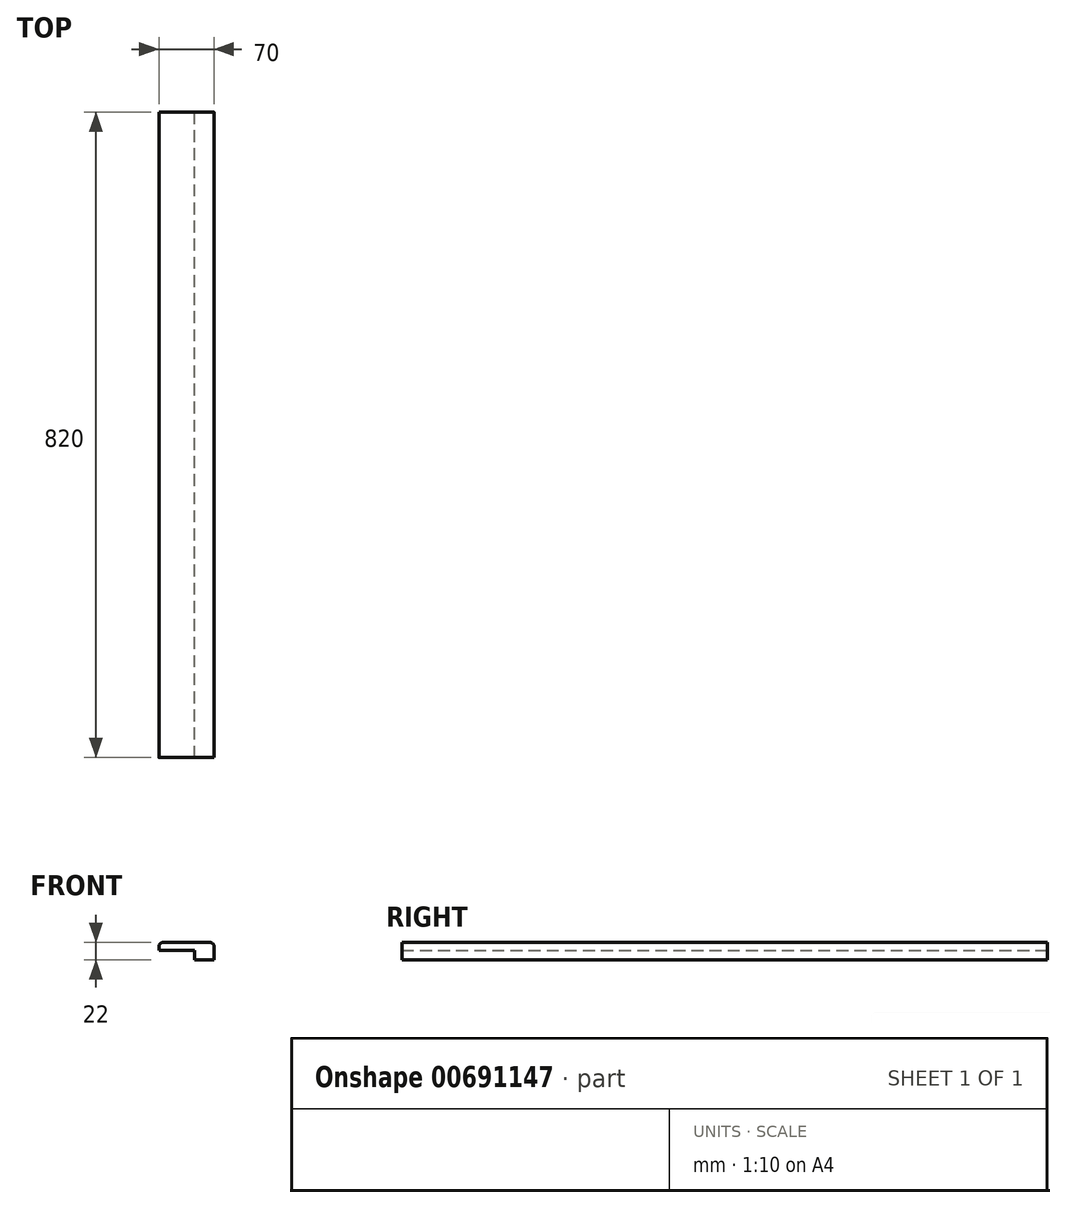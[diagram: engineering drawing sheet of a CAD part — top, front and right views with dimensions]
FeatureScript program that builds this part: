
annotation { "Feature Type Name" : "Feature", "Feature Type Description" : "" }
export const myFeature = defineFeature(function(context is Context, id is Id, definition is map)
    precondition{}
    {
        {
            var Q0;
            Q0=qCreatedBy(makeId("Front.planeOp"),FACE);
            var sketch = newSketch(context, id + "F0", { "sketchPlane" : qUnion([Q0])});
            skLineSegment(sketch, "E0", {"start": v(0, 0) * mm, "end": v(0, 5) * mm});
            skArc(sketch, "E1", {"start": v(0, 5) * mm, "mid": v(1.46, 8.54) * mm, "end": v(5, 10) * mm});
            skLineSegment(sketch, "E2", {"start": v(5, 10) * mm, "end": v(65, 10) * mm});
            skArc(sketch, "E3", {"start": v(65, 10) * mm, "mid": v(68.54, 8.54) * mm, "end": v(70, 5) * mm});
            skLineSegment(sketch, "E4", {"start": v(70, 5) * mm, "end": v(70, -12) * mm});
            skLineSegment(sketch, "E5", {"start": v(0, 0) * mm, "end": v(45, 0) * mm});
            skLineSegment(sketch, "E6", {"start": v(45, 0) * mm, "end": v(45, -12) * mm});
            skLineSegment(sketch, "E7", {"start": v(45, -12) * mm, "end": v(70, -12) * mm});
            skSolve(sketch);
        }
        {
            var Q0;
            Q0 = qSketchRegion(id + "F0", true);
            extrude(context, id + "F1", {"entities" : qUnion([Q0]), "depth" : 820 * mm, "offsetDistance" : 25 * mm});
        }
    });
